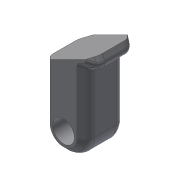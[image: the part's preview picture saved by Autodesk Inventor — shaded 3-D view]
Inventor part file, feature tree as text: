
AUTODESK INVENTOR PART (.ipt)
format: ipt  version: 2018 (Build 220112000, 112)  size: 676,352 bytes
history: native  units: mm
features: sketch x28, extrude x25, projected_geometry x25, fillet x5, hole x3, chamfer x3, mirror x1, plane x1
ambient origin geometry x8: Origin, YZ Plane, XZ Plane, XY Plane, X Axis, Y Axis, Z Axis, Center Point
bodies: Solid1 (feature_tree)
feature tree (91):
  extrude  "Extrusion1"  Depth=45.0mm
  extrude  "Extrusion2"  Depth=2.25mm
  hole  "Hole1"  [1 undecoded]
  hole  "Hole2"  [1 undecoded]
  fillet  "Fillet1"  Radius=14.0mm
  extrude  "Extrusion3"  Depth=18.5mm
  extrude  "Extrusion4"  Depth=20.5mm
  extrude  "Extrusion5"  Depth=2.195mm
  extrude  "Extrusion6"  Depth=20.5mm
  hole  "Hole3"  [1 undecoded]
  extrude  "Extrusion7"  Depth=0.5mm
  extrude  "Extrusion8"  Depth=5.0mm TaperAngle=0.0deg
  extrude  "Extrusion9"  Depth=24.5mm
  extrude  "Extrusion10"  Depth=10.0mm
  extrude  "Extrusion11"  Depth=14.5mm
  extrude  "Extrusion12"  Depth=14.5mm
  extrude  "Extrusion13"  Depth=5.0mm
  extrude  "Extrusion14"  Depth=2.25mm
  extrude  "Extrusion15"  Depth=5.0mm
  extrude  "Extrusion16"  Depth=9.0mm
  extrude  "Extrusion17"  Depth=4.0mm
  chamfer  "Chamfer1"  Distance=1.0mm
  fillet  "Fillet7"  Radius=20.7mm
  fillet  "Fillet8"  Radius=32.0mm
  mirror  "Mirror1"
  extrude  "Extrusion24"  Depth=1.0mm TaperAngle=0.0deg
  extrude  "Extrusion25"  Depth=8.0mm
  extrude  "Extrusion26"  Depth=0.2mm TaperAngle=0.0deg
  extrude  "Extrusion27"  Depth=0.5mm TaperAngle=0.0deg
  extrude  "Extrusion28"  Depth=5.0mm TaperAngle=0.0deg
  chamfer  "Chamfer5"  Distance=5.0mm
  fillet  "Fillet18"  Radius=0.2mm
  fillet  "Fillet19"  Radius=0.2mm
  extrude  "Extrusion29"  Depth=2.5mm TaperAngle=45.0deg
  chamfer  "Chamfer6"  Distance=1.5mm
  plane  "Work Plane2"
  extrude  "Extrusion30"  Depth=0.5mm
  extrude  "Extrusion31"  Depth=40.0mm
  sketch  "Sketch1"  dims[d0=24.5mm d1=45.0mm]
  sketch  "Sketch2"  dims[d2=1.95mm d3=0.0mm d4=2.25mm]
  projected_geometry  "Projected Loop1"
  sketch  "Sketch3"  dims[d5=20.0mm d6=2.25mm]
  projected_geometry  "Projected Loop2"
  sketch  "Sketch4"  dims[d7=5.25mm d8=5.25mm d9=14.0mm]
  projected_geometry  "Projected Loop3"
  sketch  "Sketch5"  dims[d10=5.25mm d11=18.5mm]
  projected_geometry  "Projected Loop4"
  sketch  "Sketch6"  dims[d12=10.0mm d13=0.0mm d14=20.5mm]
  projected_geometry  "Projected Loop5"
  sketch  "Sketch7"  dims[d15=2.0mm d16=2.195mm]
  projected_geometry  "Projected Loop6"
  sketch  "Sketch8"  dims[d17=2.0mm]
  projected_geometry  "Projected Loop7"
  sketch  "Sketch9"  dims[d18=2.4mm d19=6.0mm d20=4.4mm d21=2.0mm d22=90.0deg d23=8.0mm d24=20.594885mm d25=20.5mm]
  projected_geometry  "Projected Loop8"
  projected_geometry  "Projected Loop9"
  sketch  "Sketch10"  dims[d26=26.65mm d27=2.0mm]
  projected_geometry  "Projected Loop10"
  projected_geometry  "Projected Loop11"
  sketch  "Sketch11"  dims[d28=2.0mm]
  projected_geometry  "Projected Loop12"
  sketch  "Sketch12"  dims[d29=2.4mm d30=6.0mm d31=4.4mm d32=2.0mm d33=90.0deg d34=8.0mm d35=20.594885mm d36=0.5mm]
  sketch  "Sketch13"  dims[d37=18.0mm d38=5.0mm d39=0.0mm]
  sketch  "Sketch14"  dims[d41=10.0mm d42=0.0mm d43=24.5mm]
  projected_geometry  "Projected Loop13"
  sketch  "Sketch15"  dims[d44=1.15mm d45=0.0mm d46=10.0mm]
  sketch  "Sketch16"  dims[d47=21.0mm d48=14.5mm]
  projected_geometry  "Projected Loop14"
  sketch  "Sketch17"  dims[d49=20.0mm d50=14.5mm]
  projected_geometry  "Projected Loop15"
  sketch  "Sketch18"  dims[d51=24.5mm d52=5.0mm]
  projected_geometry  "Projected Loop16"
  sketch  "Sketch19"  dims[d53=5.0mm d54=2.25mm]
  projected_geometry  "Projected Loop17"
  sketch  "Sketch20"  dims[d55=2.25mm d56=5.0mm]
  projected_geometry  "Projected Loop18"
  sketch  "Sketch35"  dims[d57=5.0mm d58=9.0mm]
  projected_geometry  "Projected Loop28"
  sketch  "Sketch36"  dims[d59=14.75mm d60=4.0mm d61=1.0mm d62=0.0mm d63=20.7mm]
  projected_geometry  "Projected Loop29"
  sketch  "Sketch37"  dims[d64=2.4mm d65=6.0mm d66=4.4mm d67=2.0mm d68=90.0deg d69=8.0mm d70=20.594885mm d72=32.0mm]
  sketch  "Sketch38"  dims[d73=5.0mm d74=0.0mm d75=1.0mm d76=0.0mm]
  sketch  "Sketch39"  dims[d77=12.25mm d78=0.0mm d80=8.0mm]
  projected_geometry  "Projected Loop30"
  sketch  "Sketch40"  dims[d81=4.5mm d82=0.0mm d84=0.2mm d85=0.0mm]
  projected_geometry  "Projected Loop31"
  sketch  "Sketch46"  dims[d86=21.0mm d87=0.5mm d88=0.0mm]
  projected_geometry  "Projected Loop36"
  projected_geometry  "Projected Loop37"
  sketch  "Sketch47"  dims[d91=8.0mm d92=0.0mm d93=5.0mm d94=0.0mm d95=5.0mm d96=0.0mm d98=0.2mm d99=0.0mm d100=0.2mm d101=0.0mm d102=2.5mm d103=2.0mm d104=45.0deg d105=1.5mm d114=0.5mm d187=40.0mm d188=70.0mm d189=20.0mm d190=10.0mm d191=0.0mm d192=10.0mm d193=0.0mm d194=2.0mm d195=0.0mm d196=2.0mm d197=0.0mm d198=8.0mm d199=10.0mm d200=2.0mm d201=0.0mm d204=7.0mm d205=2.0mm d206=45.0deg d207=5.0mm d208=8.0mm d209=15.0mm d210=2.0mm d211=0.0mm d212=1.5mm d213=2.0mm d214=45.0deg d273=10.0mm d274=0.0mm d275=10.0mm d276=0.0mm]
  projected_geometry  "Projected Loop38"
note: 3 required parameter values undecoded (feature->parameter linkage not recoverable at this tier; creation-order binding heuristic only, values carry confidence <= 0.55)
